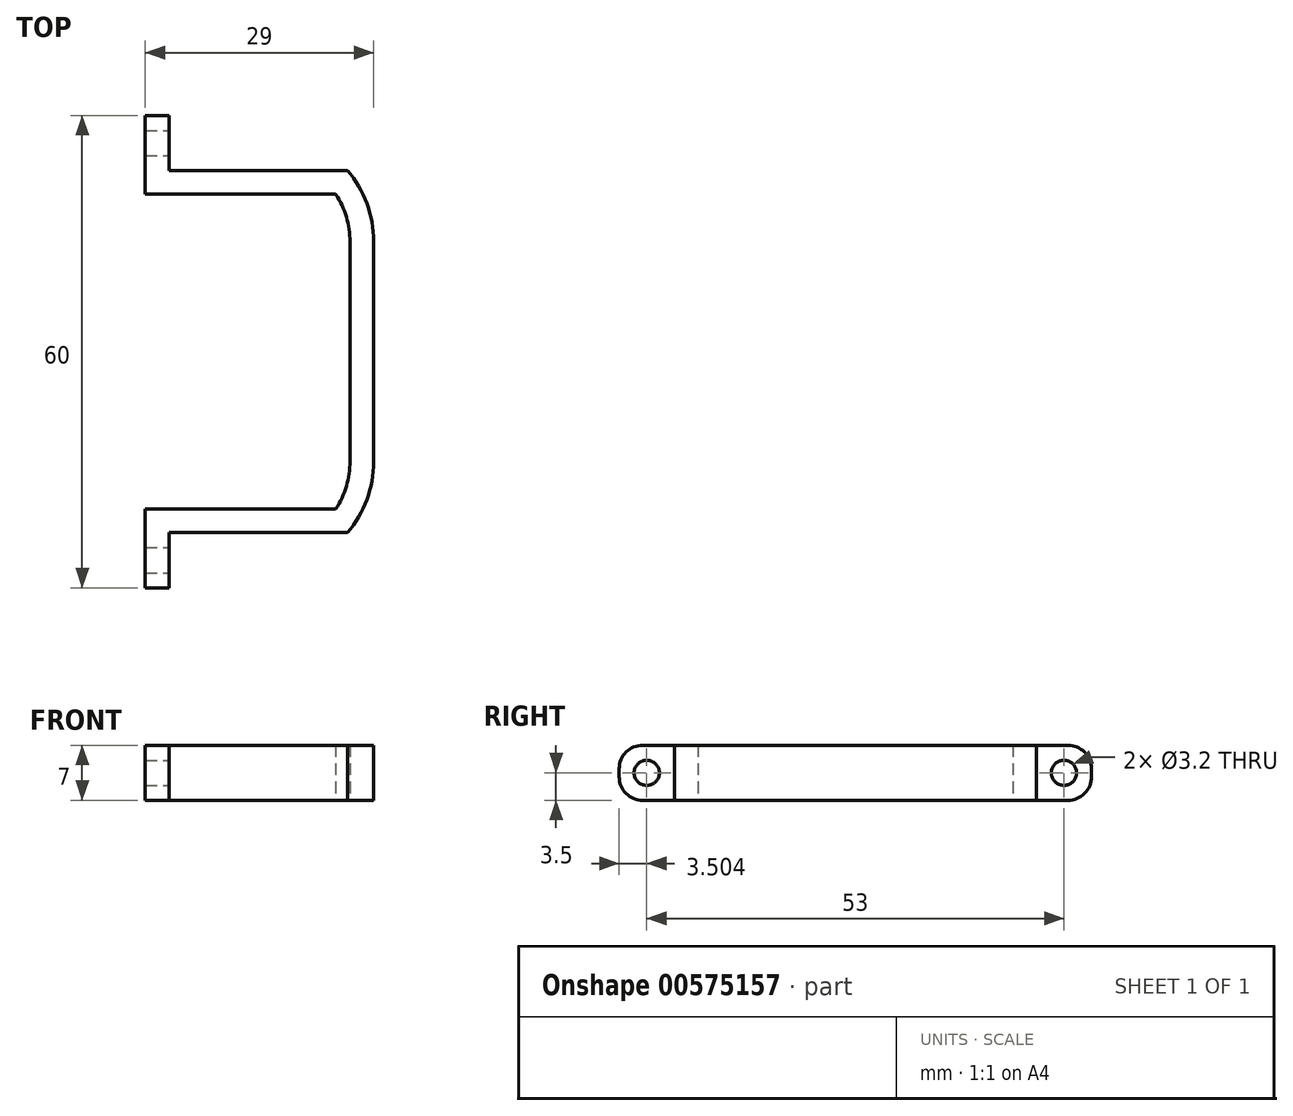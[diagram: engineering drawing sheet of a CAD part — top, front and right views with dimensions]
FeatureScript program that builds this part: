
annotation { "Feature Type Name" : "Feature", "Feature Type Description" : "" }
export const myFeature = defineFeature(function(context is Context, id is Id, definition is map)
    precondition{}
    {
        {
            var Q0;
            Q0=qCreatedBy(makeId("Top.planeOp"),FACE);
            var sketch = newSketch(context, id + "F0", { "sketchPlane" : qUnion([Q0])});
            skLineSegment(sketch, "E0", {"start": v(5.68, -16.22) * mm, "end": v(5.68, 11.66) * mm});
            skLineSegment(sketch, "E1", {"start": v(3.88, 17.72) * mm, "end": v(-20.32, 17.72) * mm});
            skLineSegment(sketch, "E2", {"start": v(3.88, -22.28) * mm, "end": v(-20.32, -22.28) * mm});
            skPoint(sketch, "E3", {"position": v(3.88, 17.72) * mm});
            skPoint(sketch, "E4", {"position": v(3.88, -22.28) * mm});
            skPoint(sketch, "E5", {"position": v(5.68, 11.72) * mm});
            skPoint(sketch, "E6", {"position": v(5.68, -16.28) * mm});
            skArc(sketch, "E7", {"start": v(5.68, 11.66) * mm, "mid": v(5.23, 14.83) * mm, "end": v(3.88, 17.72) * mm});
            skArc(sketch, "E8", {"start": v(3.88, -22.28) * mm, "mid": v(5.23, -19.38) * mm, "end": v(5.68, -16.22) * mm});
            skPoint(sketch, "E9.orphan", {"position": v(5.68, -22.28) * mm});
            skPoint(sketch, "E10.orphan", {"position": v(5.68, 17.72) * mm});
            skLineSegment(sketch, "E11.0", {"start": v(5.38, 20.72) * mm, "end": v(-20.32, 20.72) * mm});
            skLineSegment(sketch, "E11.1", {"start": v(5.38, -25.28) * mm, "end": v(-20.32, -25.28) * mm});
            skArc(sketch, "E11.2", {"start": v(5.38, -25.28) * mm, "mid": v(7.83, -21.07) * mm, "end": v(8.68, -16.28) * mm});
            skLineSegment(sketch, "E11.3", {"start": v(8.68, -16.28) * mm, "end": v(8.68, 11.73) * mm});
            skArc(sketch, "E11.4", {"start": v(8.68, 11.73) * mm, "mid": v(7.83, 16.52) * mm, "end": v(5.38, 20.72) * mm});
            skLineSegment(sketch, "E12", {"start": v(-20.32, 17.72) * mm, "end": v(-20.32, 20.72) * mm});
            skLineSegment(sketch, "E13", {"start": v(-20.32, -25.28) * mm, "end": v(-20.32, -22.28) * mm});
            skLineSegment(sketch, "E14", {"start": v(-20.32, 20.72) * mm, "end": v(-20.32, 27.72) * mm});
            skLineSegment(sketch, "E15", {"start": v(-20.32, 27.72) * mm, "end": v(-17.32, 27.72) * mm});
            skLineSegment(sketch, "E16", {"start": v(-17.32, 27.72) * mm, "end": v(-17.32, 20.72) * mm});
            skLineSegment(sketch, "E17", {"start": v(5.68, -2.28) * mm, "end": v(-36.32, -2.28) * mm, "construction": true});
            skLineSegment(sketch, "E18.MirrorCS", {"start": v(-20.32, -32.28) * mm, "end": v(-17.32, -32.28) * mm});
            skLineSegment(sketch, "E19.MirrorCS", {"start": v(-20.32, -25.28) * mm, "end": v(-20.32, -32.28) * mm});
            skLineSegment(sketch, "E20.MirrorCS", {"start": v(-17.32, -32.28) * mm, "end": v(-17.32, -25.28) * mm});
            skSolve(sketch);
        }
        {
            var Q0;
            {var subQ0=sQuery(id+"F0.wireOp",EDGE,"E14");Q0=makeQuery(id+"F0.imprint","IMPRINT",FACE,{"disambiguationData":[TD([[makeQuery(id+"F0.imprint","IMPRINT",EDGE,{"derivedFrom":subQ0}),-1.0]])]});}
            var Q1;
            Q1=makeQuery(id+"F0.imprint","IMPRINT",FACE,{"disambiguationData":[TD([[makeQuery(id+"F0.imprint","IMPRINT",EDGE,{"derivedFrom":sQuery(id+"F0.wireOp",EDGE,"E0")}),-1.0]])]});
            var Q2;
            Q2=makeQuery(id+"F0.imprint","IMPRINT",FACE,{"disambiguationData":[TD([[makeQuery(id+"F0.imprint","IMPRINT",EDGE,{"derivedFrom":sQuery(id+"F0.wireOp",EDGE,"E18.MirrorCS")}),1.0]])]});
            extrude(context, id + "F1", {"entities" : qUnion([Q0, Q1, Q2]), "depth" : 7 * mm, "offsetDistance" : 25 * mm});
        }
        {
            var Q0;
            Q0=makeQuery(id+"F1.opExtrude","CAP_EDGE",EDGE,{"disambiguationData":[OSD([sQuery(id+"F0.wireOp",EDGE,"E15")])],"isStart":true});
            var Q1;
            Q1=makeQuery(id+"F1.opExtrude","CAP_EDGE",EDGE,{"disambiguationData":[OSD([sQuery(id+"F0.wireOp",EDGE,"E15")])],"isStart":false});
            var Q2;
            Q2=makeQuery(id+"F1.opExtrude","CAP_EDGE",EDGE,{"disambiguationData":[OSD([sQuery(id+"F0.wireOp",EDGE,"E18.MirrorCS")])],"isStart":true});
            var Q3;
            Q3=makeQuery(id+"F1.opExtrude","CAP_EDGE",EDGE,{"disambiguationData":[OSD([sQuery(id+"F0.wireOp",EDGE,"E18.MirrorCS")])],"isStart":false});
            fillet(context, id + "F2", {"entities" : qUnion([Q0, Q1, Q2, Q3]), "radius" : 3 * mm, "tangentPropagation" : true, "allowEdgeOverflow" : false});
        }
        {
            var Q0;
            Q0=makeQuery(id+"F1.opExtrude","SWEPT_FACE",FACE,{"disambiguationData":[OSD([sQuery(id+"F0.wireOp",EDGE,"E20.MirrorCS")])]});
            var sketch = newSketch(context, id + "F3", { "sketchPlane" : qUnion([Q0])});
            skLineSegment(sketch, "E21", {"start": v(-32.28, 3.5) * mm, "end": v(-25.28, 3.5) * mm, "construction": true});
            skCircle(sketch, "E22", {"center": v(-28.78, 3.5) * mm, "radius": 1.6 * mm});
            skCircle(sketch, "E23", {"center": v(-28.78, 3.5) * mm, "radius": 3 * mm});
            skSolve(sketch);
        }
        {
            var Q0;
            Q0=makeQuery(id+"F3.imprint","IMPRINT",FACE,{"disambiguationData":[TD([[makeQuery(id+"F3.imprint","IMPRINT",EDGE,{"derivedFrom":sQuery(id+"F3.wireOp",EDGE,"E22")}),1.0]])]});
            extrude(context, id + "F4", {"entities" : qUnion([Q0]), "operationType" : NewBodyOperationType.REMOVE, "oppositeDirection" : true, "depth" : 25 * mm, "offsetDistance" : 25 * mm});
        }
        {
            var Q0;
            Q0=makeQuery(id+"F1.opExtrude","SWEPT_FACE",FACE,{"disambiguationData":[OSD([sQuery(id+"F0.wireOp",EDGE,"E16")])]});
            var sketch = newSketch(context, id + "F5", { "sketchPlane" : qUnion([Q0])});
            skLineSegment(sketch, "E24", {"start": v(27.72, 3.5) * mm, "end": v(20.72, 3.5) * mm, "construction": true});
            skCircle(sketch, "E25", {"center": v(24.22, 3.5) * mm, "radius": 1.6 * mm});
            skCircle(sketch, "E26", {"center": v(24.22, 3.5) * mm, "radius": 3 * mm});
            skSolve(sketch);
        }
        {
            var Q0;
            Q0=makeQuery(id+"F5.imprint","IMPRINT",FACE,{"disambiguationData":[TD([[makeQuery(id+"F5.imprint","IMPRINT",EDGE,{"derivedFrom":sQuery(id+"F5.wireOp",EDGE,"E25")}),1.0]])]});
            extrude(context, id + "F6", {"entities" : qUnion([Q0]), "operationType" : NewBodyOperationType.REMOVE, "oppositeDirection" : true, "depth" : 25 * mm, "offsetDistance" : 25 * mm});
        }
    });
